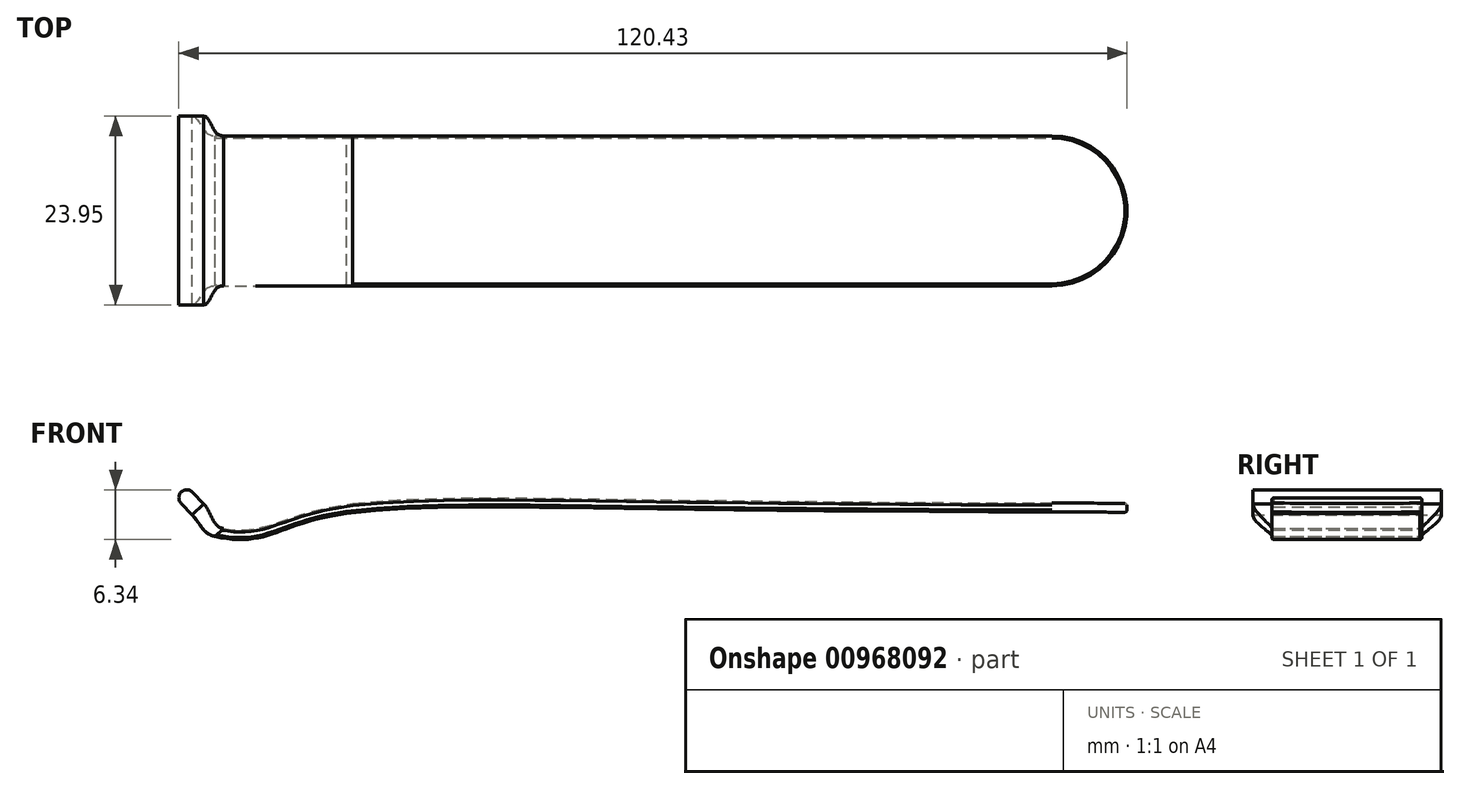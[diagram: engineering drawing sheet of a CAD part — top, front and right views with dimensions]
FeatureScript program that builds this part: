
annotation { "Feature Type Name" : "Feature", "Feature Type Description" : "" }
export const myFeature = defineFeature(function(context is Context, id is Id, definition is map)
    precondition{}
    {
        {
            var Q0;
            Q0=qCreatedBy(makeId("Front.planeOp"),FACE);
            var sketch = newSketch(context, id + "F0", { "sketchPlane" : qUnion([Q0])});
            skCircle(sketch, "E0", {"center": v(0, 0) * mm, "radius": 1.02 * mm});
            skLineSegment(sketch, "E1", {"start": v(-0.74, -0.7) * mm, "end": v(0.66, -2.17) * mm});
            skLineSegment(sketch, "E2", {"start": v(0.66, -2.17) * mm, "end": v(2.13, -0.78) * mm});
            skLineSegment(sketch, "E3", {"start": v(2.13, -0.78) * mm, "end": v(0.74, 0.7) * mm});
            skSolve(sketch);
        }
        {
            var Q0;
            Q0 = qSketchRegion(id + "F0", true);
            extrude(context, id + "F1", {"entities" : qUnion([Q0]), "depth" : 23.95 * mm, "offsetDistance" : 25.4 * mm});
        }
        {
            var Q0;
            Q0=qCreatedBy(makeId("Front.planeOp"),FACE);
            var sketch = newSketch(context, id + "F2", { "sketchPlane" : qUnion([Q0])});
            skFitSpline(sketch, "E4", {"points": [v(5.33, -3.3) * mm, v(21.56, 0) * mm], "startDerivative": vector(15.65, -2.05) * mm, "endDerivative": vector(27.49, 2.91) * mm});
            skFitSpline(sketch, "E5", {"points": [v(21.56, 0) * mm, v(123.16, 0) * mm], "startDerivative": vector(46.46, 4.55) * mm, "endDerivative": vector(223.96, 0) * mm});
            skSolve(sketch);
        }
        {
            var Q0;
            Q0=makeQuery(id+"F1.opExtrude","SWEPT_FACE",FACE,{"disambiguationData":[OSD([sQuery(id+"F0.wireOp",EDGE,"E2")])]});
            cPlane(context, id + "F3", {"entities" : qUnion([Q0]), "cplaneType" : CPlaneType.OFFSET, "offset" : 4 * mm, "width" : 152.4 * mm, "height" : 152.4 * mm});
        }
        {
            var Q0;
            Q0=qCreatedBy(id+"F3.planeOp",FACE);
            var sketch = newSketch(context, id + "F4", { "sketchPlane" : qUnion([Q0])});
            skLineSegment(sketch, "E6.0.0", {"start": v(-1.02, 0) * mm, "end": v(1.02, 0) * mm});
            skLineSegment(sketch, "E6.0.1", {"start": v(1.02, 0) * mm, "end": v(1.02, 23.95) * mm});
            skLineSegment(sketch, "E6.0.2", {"start": v(1.02, 23.95) * mm, "end": v(-1.02, 23.95) * mm});
            skLineSegment(sketch, "E6.0.3", {"start": v(-1.02, 23.95) * mm, "end": v(-1.02, 0) * mm});
            skLineSegment(sketch, "E7.bottom", {"start": v(1.02, 21.54) * mm, "end": v(-1.02, 21.54) * mm});
            skLineSegment(sketch, "E7.top", {"start": v(1.02, 2.49) * mm, "end": v(-1.02, 2.49) * mm});
            skLineSegment(sketch, "E7.left", {"start": v(1.02, 21.54) * mm, "end": v(1.02, 2.49) * mm});
            skLineSegment(sketch, "E7.right", {"start": v(-1.02, 21.54) * mm, "end": v(-1.02, 2.49) * mm});
            skLineSegment(sketch, "E8.bottom", {"start": v(0.71, 21.54) * mm, "end": v(-0.76, 21.54) * mm});
            skLineSegment(sketch, "E8.top", {"start": v(0.71, 2.49) * mm, "end": v(-0.76, 2.49) * mm});
            skLineSegment(sketch, "E8.left", {"start": v(0.71, 21.54) * mm, "end": v(0.71, 2.49) * mm});
            skLineSegment(sketch, "E8.right", {"start": v(-0.76, 21.54) * mm, "end": v(-0.76, 2.49) * mm});
            skSolve(sketch);
        }
        {
            var Q0;
            {var subQ0=sQuery(id+"F4.wireOp",EDGE,"E8.left");Q0=makeQuery(id+"F4.imprint","IMPRINT",FACE,{"disambiguationData":[TD([[makeQuery(id+"F4.imprint","IMPRINT",EDGE,{"derivedFrom":subQ0}),-1.0]])]});}
            var Q1;
            Q1 = qConstructionFilter(qBodyType(qCreatedBy(id + "F2" ,EDGE), BodyType.WIRE), ConstructionObject.NO);
            sweep(context, id + "F5", {"profiles" : qUnion([Q0]), "path" : qUnion([Q1])});
        }
        {
            var Q0;
            Q0=makeQuery(id+"F1.opExtrude","SWEPT_FACE",FACE,{"disambiguationData":[OSD([sQuery(id+"F0.wireOp",EDGE,"E2")])]});
            var Q1;
            Q1=makeQuery(id+"F5.opSweep","CAP_FACE",FACE,{"disambiguationData":[OSD([sQuery(id+"F2.wireOp",VERTEX,"E4.start"),sQuery(id+"F4.wireOp",EDGE,"E7.bottom"),sQuery(id+"F4.wireOp",EDGE,"E7.top"),sQuery(id+"F4.wireOp",EDGE,"E8.left"),sQuery(id+"F4.wireOp",EDGE,"E8.right")])],"isStart":true});
            loft(context, id + "F6", {"startCondition" : LoftEndDerivativeType.NORMAL_TO_PROFILE, "startMagnitude" : 1, "endCondition" : LoftEndDerivativeType.MATCH_CURVATURE, "endMagnitude" : 1, "sheetProfilesArray" : [{ "sheetProfileEntities" : qUnion([Q0]) }, { "sheetProfileEntities" : qUnion([Q1]) }]});
        }
        {
            var Q0;
            Q0=qCreatedBy(makeId("Top.planeOp"),FACE);
            var sketch = newSketch(context, id + "F7", { "sketchPlane" : qUnion([Q0])});
            skCircle(sketch, "E9", {"center": v(109.89, -12.01) * mm, "radius": 9.53 * mm});
            skLineSegment(sketch, "E10", {"start": v(109.89, -2.49) * mm, "end": v(127.67, -2.49) * mm});
            skLineSegment(sketch, "E11", {"start": v(127.67, -2.49) * mm, "end": v(127.67, -21.54) * mm});
            skLineSegment(sketch, "E12", {"start": v(127.67, -21.54) * mm, "end": v(109.89, -21.54) * mm});
            skSolve(sketch);
        }
        {
            var Q0;
            {var subQ0=sQuery(id+"F7.wireOp",EDGE,"E10");Q0=makeQuery(id+"F7.imprint","IMPRINT",FACE,{"disambiguationData":[TD([[makeQuery(id+"F7.imprint","IMPRINT",EDGE,{"derivedFrom":subQ0}),-1.0]])]});}
            var Q1;
            {var subQ0=sQuery(id+"F7.wireOp",EDGE,"E12");Q1=makeQuery(id+"F7.imprint","IMPRINT",FACE,{"disambiguationData":[TD([[makeQuery(id+"F7.imprint","IMPRINT",EDGE,{"derivedFrom":subQ0}),-1.0]])]});}
            extrude(context, id + "F8", {"entities" : qUnion([Q0, Q1]), "operationType" : NewBodyOperationType.REMOVE, "oppositeDirection" : true, "depth" : 25.4 * mm, "offsetDistance" : 25.4 * mm});
        }
        {
            var Q0;
            Q0=makeQuery(id+"F5.opSweep","SWEPT_EDGE",EDGE,{"disambiguationData":[OSD([sQuery(id+"F2.wireOp",EDGE,"E4"),sQuery(id+"F4.wireOp",EDGE,"E7.top"),sQuery(id+"F4.wireOp",EDGE,"E8.left")])]});
            var Q1;
            Q1=makeQuery(id+"F5.opSweep","SWEPT_EDGE",EDGE,{"disambiguationData":[OSD([sQuery(id+"F2.wireOp",EDGE,"E5"),sQuery(id+"F4.wireOp",EDGE,"E7.top"),sQuery(id+"F4.wireOp",EDGE,"E8.left")])]});
            var Q2;
            Q2=makeQuery(id+"F5.opSweep","SWEPT_EDGE",EDGE,{"disambiguationData":[OSD([sQuery(id+"F2.wireOp",EDGE,"E5"),sQuery(id+"F4.wireOp",EDGE,"E7.top"),sQuery(id+"F4.wireOp",EDGE,"E8.right")])]});
            var Q3;
            Q3=makeQuery(id+"F5.opSweep","SWEPT_EDGE",EDGE,{"disambiguationData":[OSD([sQuery(id+"F2.wireOp",EDGE,"E4"),sQuery(id+"F4.wireOp",EDGE,"E7.top"),sQuery(id+"F4.wireOp",EDGE,"E8.right")])]});
            var Q4;
            Q4=makeQuery(id+"F5.opSweep","SWEPT_EDGE",EDGE,{"disambiguationData":[OSD([sQuery(id+"F2.wireOp",EDGE,"E4"),sQuery(id+"F4.wireOp",EDGE,"E7.bottom"),sQuery(id+"F4.wireOp",EDGE,"E8.right")])]});
            var Q5;
            Q5=makeQuery(id+"F5.opSweep","SWEPT_EDGE",EDGE,{"disambiguationData":[OSD([sQuery(id+"F2.wireOp",EDGE,"E5"),sQuery(id+"F4.wireOp",EDGE,"E7.bottom"),sQuery(id+"F4.wireOp",EDGE,"E8.right")])]});
            var Q6;
            Q6=makeQuery(id+"F5.opSweep","SWEPT_EDGE",EDGE,{"disambiguationData":[OSD([sQuery(id+"F2.wireOp",EDGE,"E5"),sQuery(id+"F4.wireOp",EDGE,"E7.bottom"),sQuery(id+"F4.wireOp",EDGE,"E8.left")])]});
            var Q7;
            Q7=makeQuery(id+"F5.opSweep","SWEPT_EDGE",EDGE,{"disambiguationData":[OSD([sQuery(id+"F2.wireOp",EDGE,"E4"),sQuery(id+"F4.wireOp",EDGE,"E7.bottom"),sQuery(id+"F4.wireOp",EDGE,"E8.left")])]});
            var Q8;
            Q8=makeQuery(id+"F8.boolean.opBoolean","INTERSECT",EDGE,{"derivedFrom":[makeQuery(id+"F5.opSweep","SWEPT_FACE",FACE,{"disambiguationData":[OSD([sQuery(id+"F2.wireOp",EDGE,"E5"),sQuery(id+"F4.wireOp",EDGE,"E8.right")])]}),makeQuery(id+"F8.opExtrude","SWEPT_FACE",FACE,{"disambiguationData":[OSD([sQuery(id+"F7.wireOp",EDGE,"E9")])]})]});
            var Q9;
            Q9=makeQuery(id+"F8.boolean.opBoolean","INTERSECT",EDGE,{"derivedFrom":[makeQuery(id+"F5.opSweep","SWEPT_FACE",FACE,{"disambiguationData":[OSD([sQuery(id+"F2.wireOp",EDGE,"E5"),sQuery(id+"F4.wireOp",EDGE,"E8.left")])]}),makeQuery(id+"F8.opExtrude","SWEPT_FACE",FACE,{"disambiguationData":[OSD([sQuery(id+"F7.wireOp",EDGE,"E9")])]})]});
            var Q10;
            Q10=makeQuery(id+"F8.boolean.opBoolean","INTERSECT",EDGE,{"derivedFrom":[makeQuery(id+"F5.opSweep","SWEPT_FACE",FACE,{"disambiguationData":[OSD([sQuery(id+"F2.wireOp",EDGE,"E5"),sQuery(id+"F4.wireOp",EDGE,"E8.right")])]}),makeQuery(id+"F8.opExtrude","SWEPT_FACE",FACE,{"disambiguationData":[OSD([sQuery(id+"F7.wireOp",EDGE,"E9")])]})]});
            var Q11;
            Q11=makeQuery(id+"F8.boolean.opBoolean","INTERSECT",EDGE,{"derivedFrom":[makeQuery(id+"F5.opSweep","SWEPT_FACE",FACE,{"disambiguationData":[OSD([sQuery(id+"F2.wireOp",EDGE,"E5"),sQuery(id+"F4.wireOp",EDGE,"E8.left")])]}),makeQuery(id+"F8.opExtrude","SWEPT_FACE",FACE,{"disambiguationData":[OSD([sQuery(id+"F7.wireOp",EDGE,"E9")])]})]});
            var Q12;
            Q12=makeQuery(id+"F5.opSweep","CAP_EDGE",EDGE,{"disambiguationData":[OSD([sQuery(id+"F2.wireOp",VERTEX,"E5.end"),sQuery(id+"F4.wireOp",EDGE,"E8.right")])],"isStart":false});
            fillet(context, id + "F9", {"entities" : qUnion([Q0, Q1, Q2, Q3, Q4, Q5, Q6, Q7, Q8, Q9, Q10, Q11, Q12]), "radius" : 0.25 * mm, "tangentPropagation" : true, "allowEdgeOverflow" : false});
        }
    });
